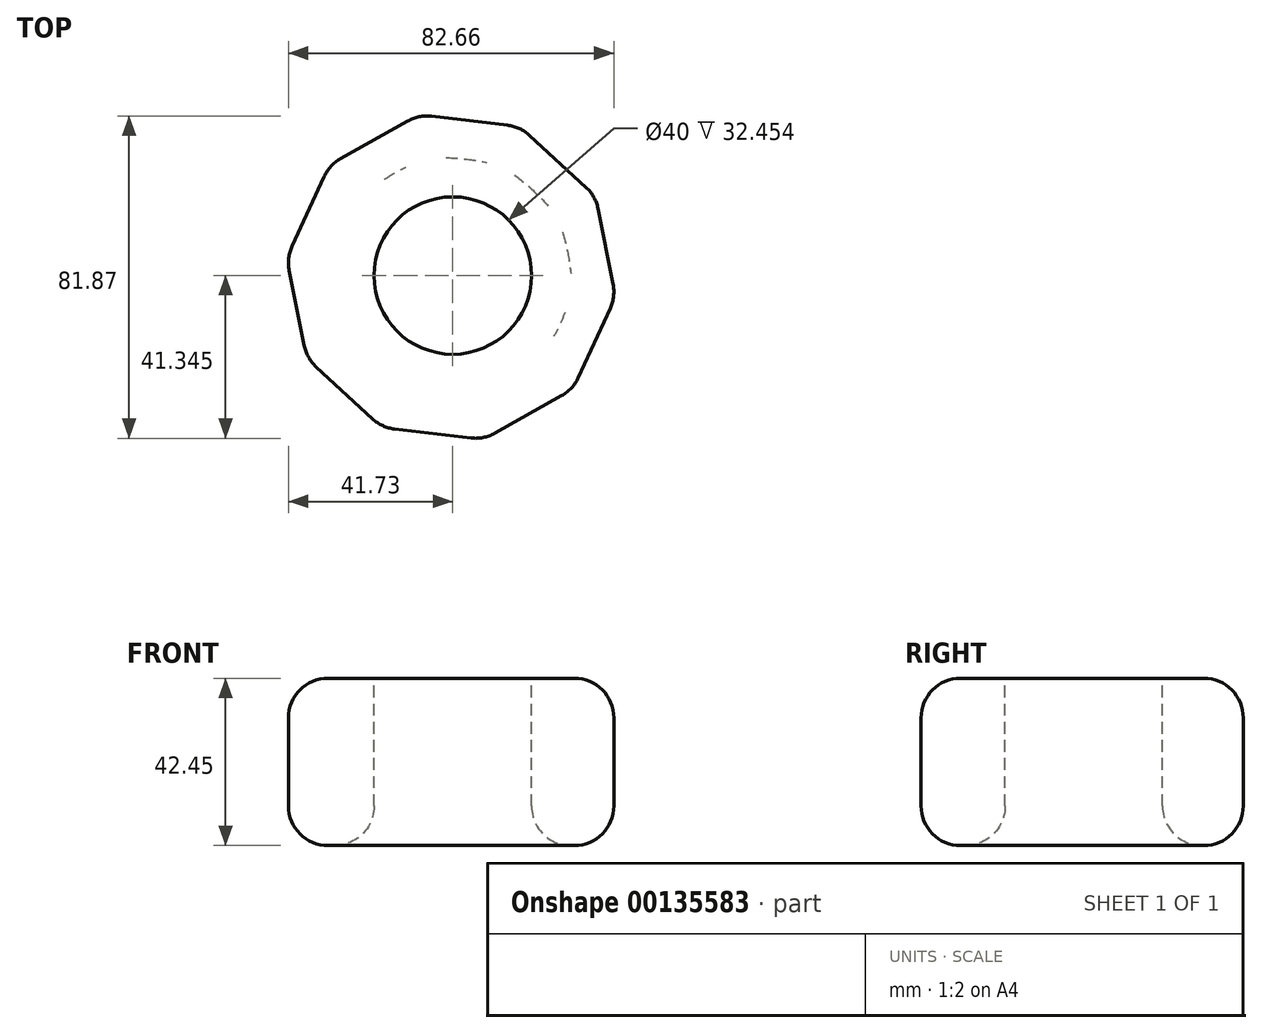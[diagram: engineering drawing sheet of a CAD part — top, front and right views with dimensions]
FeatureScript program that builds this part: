
annotation { "Feature Type Name" : "Feature", "Feature Type Description" : "" }
export const myFeature = defineFeature(function(context is Context, id is Id, definition is map)
    precondition{}
    {
        {
            var Q0;
            Q0=qCreatedBy(makeId("Top.planeOp"),FACE);
            var sketch = newSketch(context, id + "F0", { "sketchPlane" : qUnion([Q0])});
            skCircle(sketch, "E0.cCircle", {"center": v(-36.34, 47) * mm, "radius": 40 * mm, "construction": true});
            skLineSegment(sketch, "E0.0", {"start": v(5.43, 42.1) * mm, "end": v(-5.43, 18.48) * mm});
            skLineSegment(sketch, "E0.1", {"start": v(-5.43, 18.48) * mm, "end": v(-28.1, 5.75) * mm});
            skLineSegment(sketch, "E0.2", {"start": v(-28.1, 5.75) * mm, "end": v(-53.91, 8.78) * mm});
            skLineSegment(sketch, "E0.3", {"start": v(-53.91, 8.78) * mm, "end": v(-73.02, 26.4) * mm});
            skLineSegment(sketch, "E0.4", {"start": v(-73.02, 26.4) * mm, "end": v(-78.11, 51.9) * mm});
            skLineSegment(sketch, "E0.5", {"start": v(-78.11, 51.9) * mm, "end": v(-67.26, 75.51) * mm});
            skLineSegment(sketch, "E0.6", {"start": v(-67.26, 75.51) * mm, "end": v(-44.6, 88.24) * mm});
            skLineSegment(sketch, "E0.7", {"start": v(-44.6, 88.24) * mm, "end": v(-18.77, 85.2) * mm});
            skLineSegment(sketch, "E0.8", {"start": v(-18.77, 85.2) * mm, "end": v(0.33, 67.58) * mm});
            skLineSegment(sketch, "E0.9", {"start": v(0.33, 67.58) * mm, "end": v(5.43, 42.1) * mm});
            skPoint(sketch, "E0.0.midPoint", {"position": v(0, 30.29) * mm});
            skSolve(sketch);
        }
        {
            var Q0;
            Q0 = qSketchRegion(id + "F0", true);
            extrude(context, id + "F1", {"entities" : qUnion([Q0]), "depth" : 42.45 * mm});
        }
        {
            var Q0;
            Q0=makeQuery(id+"F1.opExtrude","CAP_FACE",FACE,{"disambiguationData":[OSD([sQuery(id+"F0.wireOp",EDGE,"E0.0"),sQuery(id+"F0.wireOp",EDGE,"E0.1"),sQuery(id+"F0.wireOp",EDGE,"E0.2"),sQuery(id+"F0.wireOp",EDGE,"E0.3"),sQuery(id+"F0.wireOp",EDGE,"E0.4"),sQuery(id+"F0.wireOp",EDGE,"E0.5"),sQuery(id+"F0.wireOp",EDGE,"E0.6"),sQuery(id+"F0.wireOp",EDGE,"E0.7"),sQuery(id+"F0.wireOp",EDGE,"E0.8"),sQuery(id+"F0.wireOp",EDGE,"E0.9")])],"isStart":false});
            var sketch = newSketch(context, id + "F2", { "sketchPlane" : qUnion([Q0])});
            skCircle(sketch, "E1", {"center": v(-35.94, 47.4) * mm, "radius": 20 * mm});
            skSolve(sketch);
        }
        {
            var Q0;
            Q0 = qSketchRegion(id + "F2", true);
            extrude(context, id + "F3", {"entities" : qUnion([Q0]), "operationType" : NewBodyOperationType.ADD, "depth" : 25 * mm});
        }
        {
            var Q0;
            Q0=makeQuery(id+"F3.opExtrude","CAP_FACE",FACE,{"disambiguationData":[OSD([sQuery(id+"F2.wireOp",EDGE,"E1")])],"isStart":false});
            extrude(context, id + "F4", {"entities" : qUnion([Q0]), "operationType" : NewBodyOperationType.REMOVE, "oppositeDirection" : true, "depth" : 75 * mm});
        }
        {
            var Q0;
            Q0=makeQuery(id+"F1.opExtrude","CAP_EDGE",EDGE,{"disambiguationData":[OSD([sQuery(id+"F0.wireOp",EDGE,"E0.2")])],"isStart":false});
            var Q1;
            Q1=makeQuery(id+"F1.opExtrude","CAP_EDGE",EDGE,{"disambiguationData":[OSD([sQuery(id+"F0.wireOp",EDGE,"E0.3")])],"isStart":false});
            var Q2;
            Q2=makeQuery(id+"F1.opExtrude","CAP_EDGE",EDGE,{"disambiguationData":[OSD([sQuery(id+"F0.wireOp",EDGE,"E0.8")])],"isStart":true});
            var Q3;
            Q3=makeQuery(id+"F1.opExtrude","SWEPT_EDGE",EDGE,{"disambiguationData":[OSD([sQuery(id+"F0.wireOp",EDGE,"E0.3"),sQuery(id+"F0.wireOp",EDGE,"E0.4")])]});
            var Q4;
            Q4=makeQuery(id+"F1.opExtrude","SWEPT_EDGE",EDGE,{"disambiguationData":[OSD([sQuery(id+"F0.wireOp",EDGE,"E0.6"),sQuery(id+"F0.wireOp",EDGE,"E0.7")])]});
            var Q5;
            Q5=makeQuery(id+"F1.opExtrude","SWEPT_EDGE",EDGE,{"disambiguationData":[OSD([sQuery(id+"F0.wireOp",EDGE,"E0.7"),sQuery(id+"F0.wireOp",EDGE,"E0.8")])]});
            var Q6;
            Q6=makeQuery(id+"F1.opExtrude","SWEPT_EDGE",EDGE,{"disambiguationData":[OSD([sQuery(id+"F0.wireOp",EDGE,"E0.8"),sQuery(id+"F0.wireOp",EDGE,"E0.9")])]});
            var Q7;
            Q7=makeQuery(id+"F1.opExtrude","SWEPT_EDGE",EDGE,{"disambiguationData":[OSD([sQuery(id+"F0.wireOp",EDGE,"E0.5"),sQuery(id+"F0.wireOp",EDGE,"E0.6")])]});
            var Q8;
            Q8=makeQuery(id+"F3.opExtrude","CAP_EDGE",EDGE,{"disambiguationData":[OSD([sQuery(id+"F2.wireOp",EDGE,"E1")])],"isStart":true});
            var Q9;
            Q9=makeQuery(id+"F1.opExtrude","CAP_EDGE",EDGE,{"disambiguationData":[OSD([sQuery(id+"F0.wireOp",EDGE,"E0.7")])],"isStart":true});
            var Q10;
            Q10=makeQuery(id+"F1.opExtrude","SWEPT_EDGE",EDGE,{"disambiguationData":[OSD([sQuery(id+"F0.wireOp",EDGE,"E0.4"),sQuery(id+"F0.wireOp",EDGE,"E0.5")])]});
            var Q11;
            Q11=makeQuery(id+"F1.opExtrude","CAP_EDGE",EDGE,{"disambiguationData":[OSD([sQuery(id+"F0.wireOp",EDGE,"E0.7")])],"isStart":false});
            var Q12;
            Q12=makeQuery(id+"F1.opExtrude","CAP_EDGE",EDGE,{"disambiguationData":[OSD([sQuery(id+"F0.wireOp",EDGE,"E0.4")])],"isStart":false});
            var Q13;
            Q13=makeQuery(id+"F1.opExtrude","CAP_EDGE",EDGE,{"disambiguationData":[OSD([sQuery(id+"F0.wireOp",EDGE,"E0.8")])],"isStart":false});
            var Q14;
            Q14=makeQuery(id+"F1.opExtrude","CAP_EDGE",EDGE,{"disambiguationData":[OSD([sQuery(id+"F0.wireOp",EDGE,"E0.4")])],"isStart":true});
            var Q15;
            Q15=makeQuery(id+"F1.opExtrude","CAP_EDGE",EDGE,{"disambiguationData":[OSD([sQuery(id+"F0.wireOp",EDGE,"E0.5")])],"isStart":true});
            var Q16;
            Q16=makeQuery(id+"F1.opExtrude","CAP_EDGE",EDGE,{"disambiguationData":[OSD([sQuery(id+"F0.wireOp",EDGE,"E0.2")])],"isStart":true});
            var Q17;
            Q17=makeQuery(id+"F1.opExtrude","CAP_EDGE",EDGE,{"disambiguationData":[OSD([sQuery(id+"F0.wireOp",EDGE,"E0.9")])],"isStart":true});
            var Q18;
            Q18=makeQuery(id+"F1.opExtrude","CAP_EDGE",EDGE,{"disambiguationData":[OSD([sQuery(id+"F0.wireOp",EDGE,"E0.5")])],"isStart":false});
            var Q19;
            Q19=makeQuery(id+"F1.opExtrude","CAP_EDGE",EDGE,{"disambiguationData":[OSD([sQuery(id+"F0.wireOp",EDGE,"E0.0")])],"isStart":true});
            var Q20;
            Q20=makeQuery(id+"F1.opExtrude","CAP_EDGE",EDGE,{"disambiguationData":[OSD([sQuery(id+"F0.wireOp",EDGE,"E0.3")])],"isStart":true});
            var Q21;
            Q21=makeQuery(id+"F1.opExtrude","SWEPT_EDGE",EDGE,{"disambiguationData":[OSD([sQuery(id+"F0.wireOp",EDGE,"E0.0"),sQuery(id+"F0.wireOp",EDGE,"E0.1")])]});
            var Q22;
            Q22=makeQuery(id+"F1.opExtrude","SWEPT_EDGE",EDGE,{"disambiguationData":[OSD([sQuery(id+"F0.wireOp",EDGE,"E0.1"),sQuery(id+"F0.wireOp",EDGE,"E0.2")])]});
            var Q23;
            Q23=makeQuery(id+"F1.opExtrude","CAP_EDGE",EDGE,{"disambiguationData":[OSD([sQuery(id+"F0.wireOp",EDGE,"E0.1")])],"isStart":false});
            var Q24;
            Q24=makeQuery(id+"F1.opExtrude","SWEPT_EDGE",EDGE,{"disambiguationData":[OSD([sQuery(id+"F0.wireOp",EDGE,"E0.2"),sQuery(id+"F0.wireOp",EDGE,"E0.3")])]});
            var Q25;
            Q25=makeQuery(id+"F1.opExtrude","SWEPT_EDGE",EDGE,{"disambiguationData":[OSD([sQuery(id+"F0.wireOp",EDGE,"E0.0"),sQuery(id+"F0.wireOp",EDGE,"E0.9")])]});
            var Q26;
            Q26=makeQuery(id+"F1.opExtrude","CAP_EDGE",EDGE,{"disambiguationData":[OSD([sQuery(id+"F0.wireOp",EDGE,"E0.0")])],"isStart":false});
            var Q27;
            Q27=makeQuery(id+"F1.opExtrude","CAP_EDGE",EDGE,{"disambiguationData":[OSD([sQuery(id+"F0.wireOp",EDGE,"E0.1")])],"isStart":true});
            var Q28;
            Q28=makeQuery(id+"F1.opExtrude","CAP_EDGE",EDGE,{"disambiguationData":[OSD([sQuery(id+"F0.wireOp",EDGE,"E0.6")])],"isStart":true});
            var Q29;
            Q29=makeQuery(id+"F1.opExtrude","CAP_EDGE",EDGE,{"disambiguationData":[OSD([sQuery(id+"F0.wireOp",EDGE,"E0.9")])],"isStart":false});
            var Q30;
            Q30=makeQuery(id+"F4.boolean.opBoolean","INTERSECT",EDGE,{"derivedFrom":[makeQuery(id+"F1.opExtrude","CAP_FACE",FACE,{"disambiguationData":[OSD([sQuery(id+"F0.wireOp",EDGE,"E0.0"),sQuery(id+"F0.wireOp",EDGE,"E0.1"),sQuery(id+"F0.wireOp",EDGE,"E0.2"),sQuery(id+"F0.wireOp",EDGE,"E0.3"),sQuery(id+"F0.wireOp",EDGE,"E0.4"),sQuery(id+"F0.wireOp",EDGE,"E0.5"),sQuery(id+"F0.wireOp",EDGE,"E0.6"),sQuery(id+"F0.wireOp",EDGE,"E0.7"),sQuery(id+"F0.wireOp",EDGE,"E0.8"),sQuery(id+"F0.wireOp",EDGE,"E0.9")])],"isStart":true}),makeQuery(id+"F4.opExtrude","SWEPT_FACE",FACE,{"disambiguationData":[OSD([sQuery(id+"F2.wireOp",EDGE,"E1")])]})]});
            var Q31;
            Q31=makeQuery(id+"F1.opExtrude","CAP_EDGE",EDGE,{"disambiguationData":[OSD([sQuery(id+"F0.wireOp",EDGE,"E0.6")])],"isStart":false});
            fillet(context, id + "F5", {"entities" : qUnion([Q0, Q1, Q2, Q3, Q4, Q5, Q6, Q7, Q8, Q9, Q10, Q11, Q12, Q13, Q14, Q15, Q16, Q17, Q18, Q19, Q20, Q21, Q22, Q23, Q24, Q25, Q26, Q27, Q28, Q29, Q30, Q31]), "radius" : 10 * mm, "tangentPropagation" : true, "allowEdgeOverflow" : false});
        }
    });
